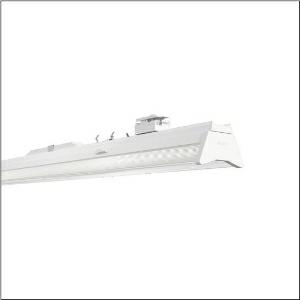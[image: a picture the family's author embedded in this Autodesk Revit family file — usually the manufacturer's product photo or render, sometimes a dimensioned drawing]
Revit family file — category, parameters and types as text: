
# Revit family: licross_11_performance_ho_51tm16mn4gxm
name_source: partatom
category: Lighting Fixtures
units: mm (PartAtom-declared; Revit-internal decimal feet)

## family parameters
Cut with Voids When Loaded = No
Host = Face
Light Source = No
Part Type = Normal
Room Calculation Point = No
Round Connector Dimension = Use Diameter
Shared = No

## types (1)
- --- (1 x LED, 16020 lm, 87.4 W, 4000K)
    Apparent Load = 87 VA
    CIE Flux Codes = 63 87 95 78 100
    Color Rendering = 80
    Color Temperature = 4000K
    Default Elevation = 1800 mm
    Description = Licross 11 Performance HO, luminaire insert, of sheet steel, galvanised, coil coated, white, length: 1.500mm, width: 120mm, height: 123mm, LED rated luminous flux: 16.020lm, light colour: 840, SDCM (Standard Deviation of Colour Matching)MacAdam ≤ 2 SDCM (initial), control gear: ON/OFF Multilumen, with plug, 3-pole, with phase selection, mains connection: 220..240V, AC, 50/60Hz, rated input power: 87W, internal wiring halogen-free, primary light control with lens, of plastic, primary optical cover: cover, of PMMA, light emission: direct/indirect distribution, primary light characteristic: symmetric, protection rating (complete): IP40, insulation class (complete): insulation class I (protective earthing), certification: CE, ENEC, VDE, UKCA, protection symbol: D if used in an environment without relevant dust loads with corresponding accessories, impact resistance: IK06, permissible ambient temperature for indoor applications: -35..+35°C, corresponds to IFS (International Featured Standards) requirements for safety and quality in the food industry, reducing of maximum allowable ambient temperature of 5°C with ceiling mounting, LABS conformity tested according to VDMA 24364:2018-05, The light source and the operating device comply with the requirements of the Ecodesign Regulation (EU) 2019/2020 and are replaceable in accordance with this regulation, packaging unit: 1 piece
    Height = 114 mm
    Lamp = 1 x LED
    Lamp Light Flux = 16020 lm
    Lamp Power = 87.4 W
    Lamp count = 1
    Length = 1500 mm
    Luminous efficacy = 183 lm/W
    Manufacturer = Siteco
    ModVariant = No
    Model = 51TM16MN4GXM
    Mounting Place = Ceiling
    Mounting Type = Pendant
    Number of Poles = 1
    OnlyDefault = Yes
    Power Factor = 1
    Product Name = Licross 11 Performance HO
    Product group = luminaire insert | ceiling pendant
    ProductGroupID = 901
    Protection Class = Protection class I
    Protection Degree = IP 40
    RLX_Detail_Level = 1
    RLX_Emergency_Light_Flux = 0 lm
    RLX_Emergency_Type = 0
    RLX_Emergency_Type_DB = No
    RlxData = <blob elided: 32037 chars, md5=027b8be7>
    Socket = socket
    Standby Power = 0 W
    System Light Flux = 16020 lm
    System Power = 87 W
    Type Comments = factory setting: luminous flux: 100 % | (A | C | E) | 203 mA
    Type Image = l_1256138.jpg
    URL = http://relux.com
    VarID = @adj_090607
    Voltage = 0 V
    Weight = 0.00 kg
    Width = 120 mm

## geometry (parser evidence)
native form markers: Blend x4, Sweep x13
no freeform markers — native parametric forms only
